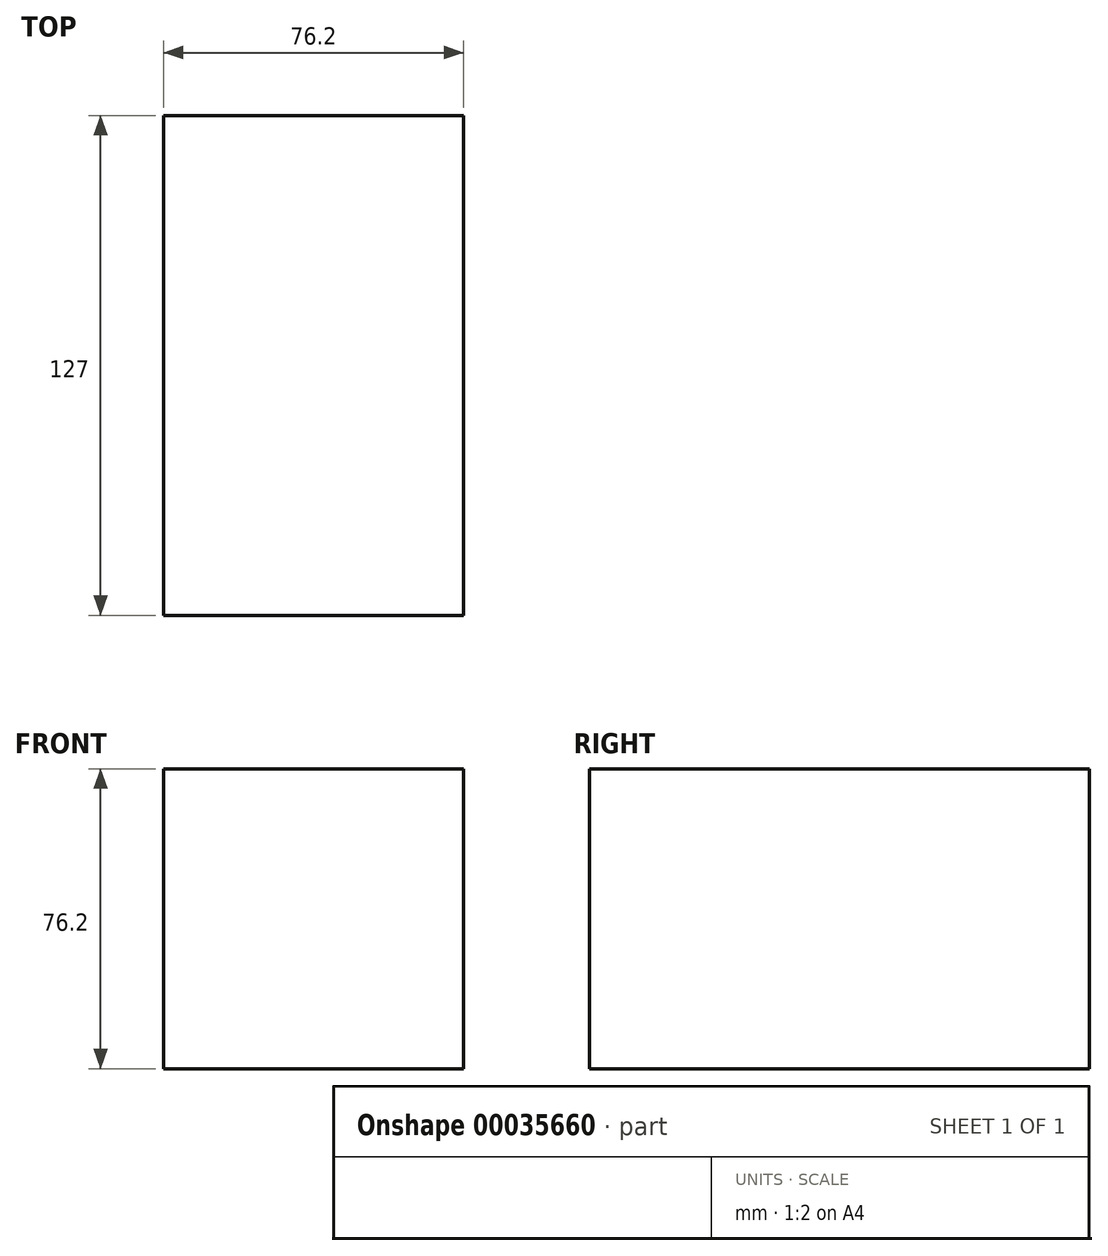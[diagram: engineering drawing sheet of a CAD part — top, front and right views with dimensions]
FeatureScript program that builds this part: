
annotation { "Feature Type Name" : "Feature", "Feature Type Description" : "" }
export const myFeature = defineFeature(function(context is Context, id is Id, definition is map)
    precondition{}
    {
        {
            var Q0;
            Q0=qCreatedBy(makeId("Front.planeOp"),FACE);
            var sketch = newSketch(context, id + "F0", { "sketchPlane" : qUnion([Q0])});
            skLineSegment(sketch, "E0.bottom", {"start": v(-46.52, 40.47) * mm, "end": v(29.68, 40.47) * mm});
            skLineSegment(sketch, "E0.top", {"start": v(-46.52, -35.73) * mm, "end": v(29.68, -35.73) * mm});
            skLineSegment(sketch, "E0.left", {"start": v(-46.52, 40.47) * mm, "end": v(-46.52, -35.73) * mm});
            skLineSegment(sketch, "E0.right", {"start": v(29.68, 40.47) * mm, "end": v(29.68, -35.73) * mm});
            skSolve(sketch);
        }
        {
            var Q0;
            Q0=makeQuery(id+"F0.imprint","IMPRINT",FACE,{"disambiguationData":[TD([[makeQuery(id+"F0.imprint","IMPRINT",EDGE,{"derivedFrom":sQuery(id+"F0.wireOp",EDGE,"E0.bottom")}),-1.0]])]});
            extrude(context, id + "F1", {"entities" : qUnion([Q0]), "depth" : 127 * mm});
        }
    });
